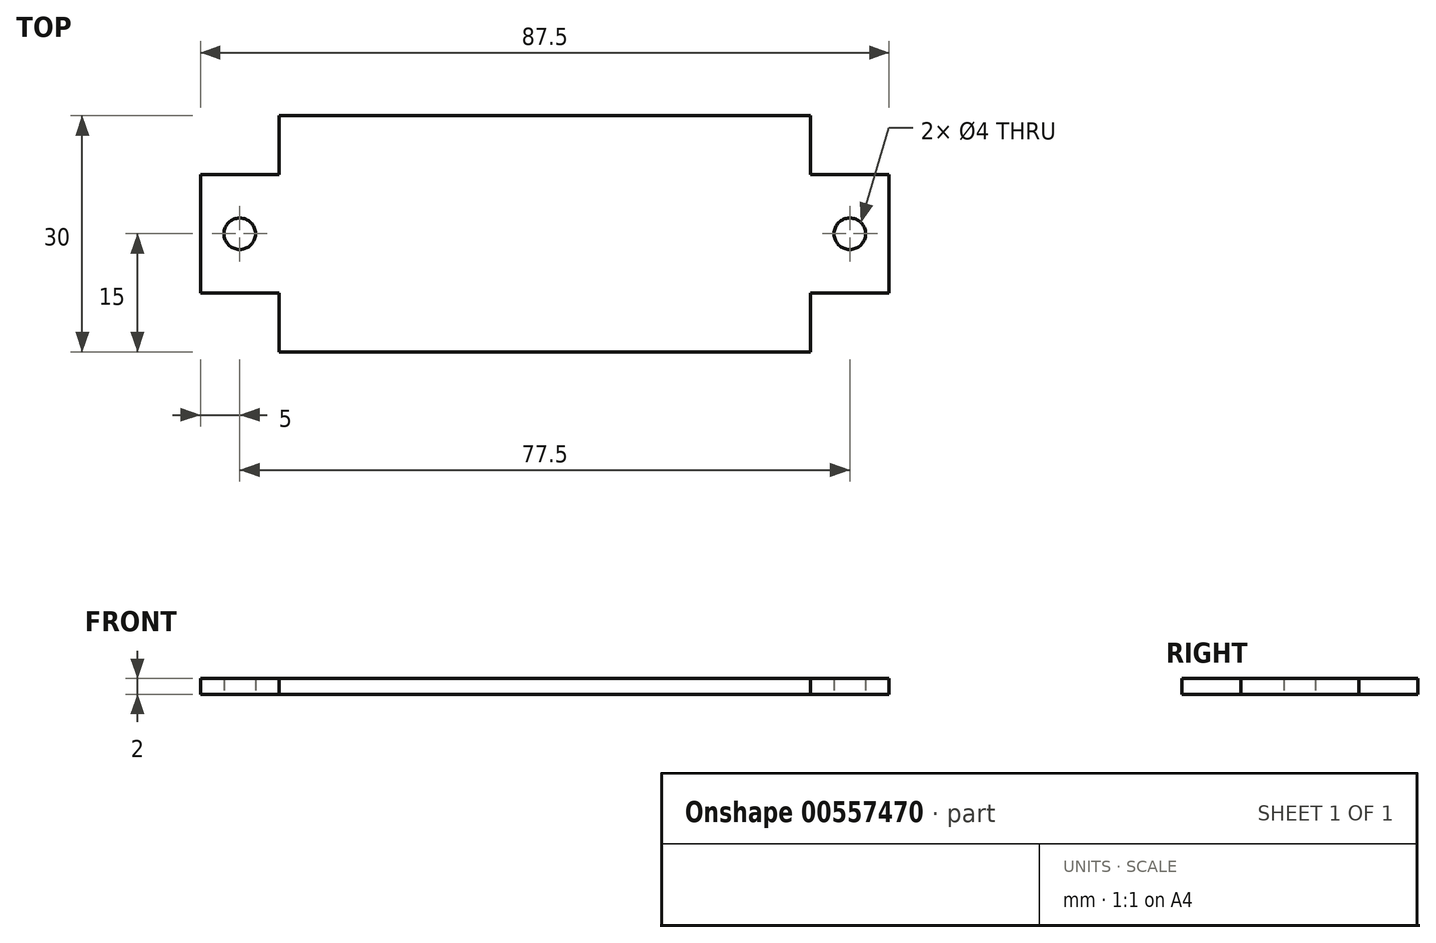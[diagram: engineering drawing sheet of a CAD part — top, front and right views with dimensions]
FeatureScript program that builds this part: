
annotation { "Feature Type Name" : "Feature", "Feature Type Description" : "" }
export const myFeature = defineFeature(function(context is Context, id is Id, definition is map)
    precondition{}
    {
        {
            var Q0;
            Q0=qCreatedBy(makeId("Top.planeOp"),FACE);
            var sketch = newSketch(context, id + "F0", { "sketchPlane" : qUnion([Q0])});
            skLineSegment(sketch, "E0.bottom", {"start": v(33.75, -15) * mm, "end": v(-33.75, -15) * mm});
            skLineSegment(sketch, "E0.top", {"start": v(33.75, 15) * mm, "end": v(-33.75, 15) * mm});
            skLineSegment(sketch, "E0.left", {"start": v(33.75, -15) * mm, "end": v(33.75, 15) * mm});
            skLineSegment(sketch, "E0.right", {"start": v(-33.75, -15) * mm, "end": v(-33.75, 15) * mm});
            skPoint(sketch, "E0.middle", {"position": v(0, 0) * mm});
            skLineSegment(sketch, "E1", {"start": v(-43.75, -7.5) * mm, "end": v(-43.75, 7.5) * mm});
            skLineSegment(sketch, "E2", {"start": v(-43.75, 7.5) * mm, "end": v(-33.75, 7.5) * mm});
            skLineSegment(sketch, "E3", {"start": v(-43.75, -7.5) * mm, "end": v(-33.75, -7.5) * mm});
            skLineSegment(sketch, "E4.MirrorCS", {"start": v(43.75, 7.5) * mm, "end": v(33.75, 7.5) * mm});
            skLineSegment(sketch, "E5.MirrorCS", {"start": v(43.75, -7.5) * mm, "end": v(43.75, 7.5) * mm});
            skLineSegment(sketch, "E6.MirrorCS", {"start": v(43.75, -7.5) * mm, "end": v(33.75, -7.5) * mm});
            skCircle(sketch, "E7", {"center": v(-38.75, 0) * mm, "radius": 2 * mm});
            skCircle(sketch, "E8", {"center": v(38.75, 0) * mm, "radius": 2 * mm});
            skSolve(sketch);
        }
        {
            var Q0;
            {var subQ3=sQuery(id+"F0.wireOp",EDGE,"E0.bottom");Q0=makeQuery(id+"F0.imprint","IMPRINT",FACE,{"disambiguationData":[TD([[makeQuery(id+"F0.imprint","IMPRINT",EDGE,{"derivedFrom":subQ3}),-1.0]])]});}
            var Q1;
            Q1=makeQuery(id+"F0.imprint","IMPRINT",FACE,{"disambiguationData":[TD([[makeQuery(id+"F0.imprint","IMPRINT",EDGE,{"derivedFrom":sQuery(id+"F0.wireOp",EDGE,"E1")}),-1.0]])]});
            var Q2;
            {var subQ0=sQuery(id+"F0.wireOp",EDGE,"E4.MirrorCS");Q2=makeQuery(id+"F0.imprint","IMPRINT",FACE,{"disambiguationData":[TD([[makeQuery(id+"F0.imprint","IMPRINT",EDGE,{"derivedFrom":subQ0}),1.0]])]});}
            extrude(context, id + "F1", {"entities" : qUnion([Q0, Q1, Q2]), "depth" : 2 * mm, "offsetDistance" : 25 * mm});
        }
    });
